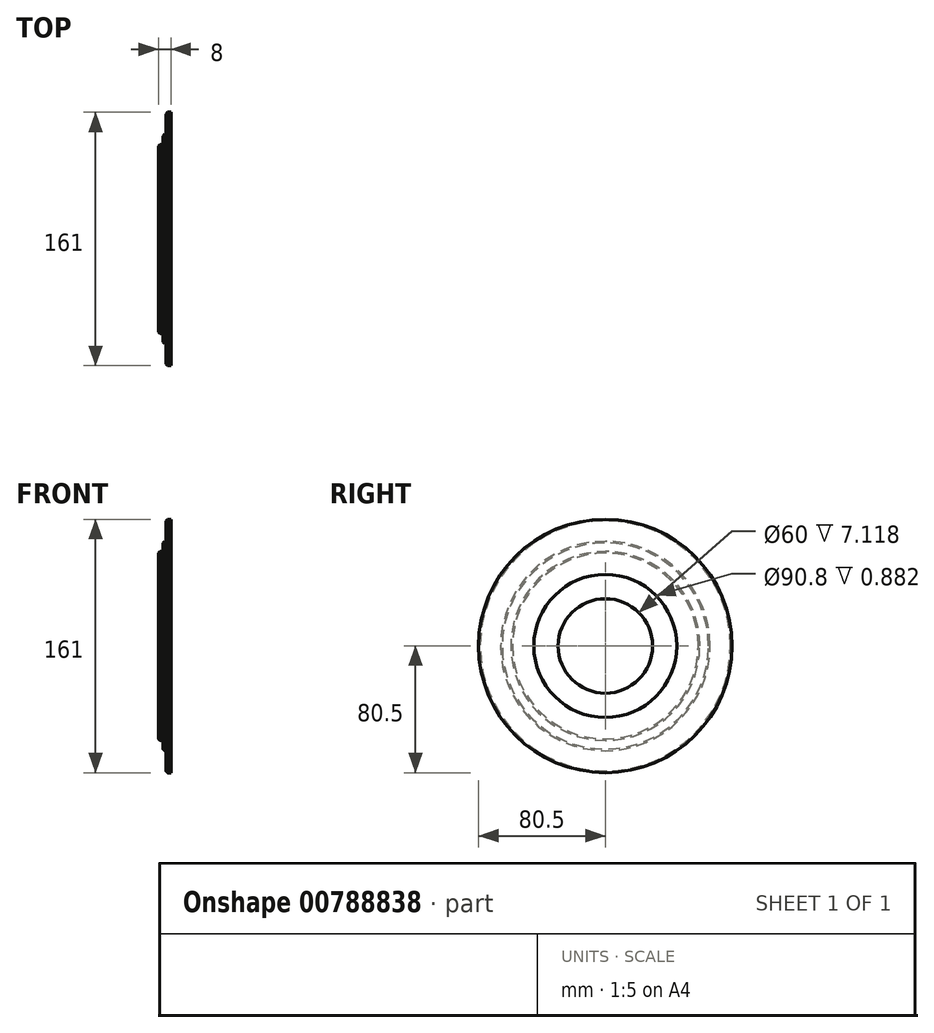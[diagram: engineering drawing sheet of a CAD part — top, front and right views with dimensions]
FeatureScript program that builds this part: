
annotation { "Feature Type Name" : "Feature", "Feature Type Description" : "" }
export const myFeature = defineFeature(function(context is Context, id is Id, definition is map)
    precondition{}
    {
        {
            var Q0;
            Q0=qCreatedBy(makeId("Front.planeOp"),FACE);
            var sketch = newSketch(context, id + "F0", { "sketchPlane" : qUnion([Q0])});
            skLineSegment(sketch, "E0", {"start": v(0, 0) * mm, "end": v(0, 59) * mm});
            skLineSegment(sketch, "E1", {"start": v(1, 60) * mm, "end": v(2.84, 60) * mm});
            skLineSegment(sketch, "E2", {"start": v(2.84, 60) * mm, "end": v(2.84, 65.5) * mm});
            skLineSegment(sketch, "E3", {"start": v(3.84, 66.5) * mm, "end": v(4.84, 66.5) * mm});
            skLineSegment(sketch, "E4", {"start": v(4.84, 66.5) * mm, "end": v(4.84, 79.5) * mm});
            skLineSegment(sketch, "E5", {"start": v(5.84, 80.5) * mm, "end": v(8, 80.5) * mm});
            skLineSegment(sketch, "E6", {"start": v(8, 80.5) * mm, "end": v(8, 45.4) * mm});
            skLineSegment(sketch, "E7", {"start": v(8, 0) * mm, "end": v(0, 0) * mm});
            skLineSegment(sketch, "E8", {"start": v(0, 30) * mm, "end": v(7.12, 30) * mm});
            skLineSegment(sketch, "E9", {"start": v(7.12, 30) * mm, "end": v(7.12, 45.4) * mm});
            skLineSegment(sketch, "E10", {"start": v(7.12, 45.4) * mm, "end": v(8, 45.4) * mm});
            skLineSegment(sketch, "E11", {"start": v(4.84, 79.5) * mm, "end": v(5.84, 80.5) * mm});
            skPoint(sketch, "E12.orphan", {"position": v(4.84, 80.5) * mm});
            skLineSegment(sketch, "E13", {"start": v(2.84, 65.5) * mm, "end": v(3.84, 66.5) * mm});
            skPoint(sketch, "E14.orphan", {"position": v(2.84, 66.5) * mm});
            skLineSegment(sketch, "E15", {"start": v(0, 59) * mm, "end": v(1, 60) * mm});
            skPoint(sketch, "E16.orphan", {"position": v(0, 60) * mm});
            skSolve(sketch);
        }
        {
            var Q0;
            Q0 = qSketchRegion(id + "F0", true);
            var Q1;
            Q1=sQuery(id+"F0.wireOp",EDGE,"E7");
            revolve(context, id + "F1", {"surfaceOperationType" : NewSurfaceOperationType.NEW, "entities" : qUnion([Q0]), "axis" : qUnion([Q1]), "revolveType" : RevolveType.FULL});
        }
    });
